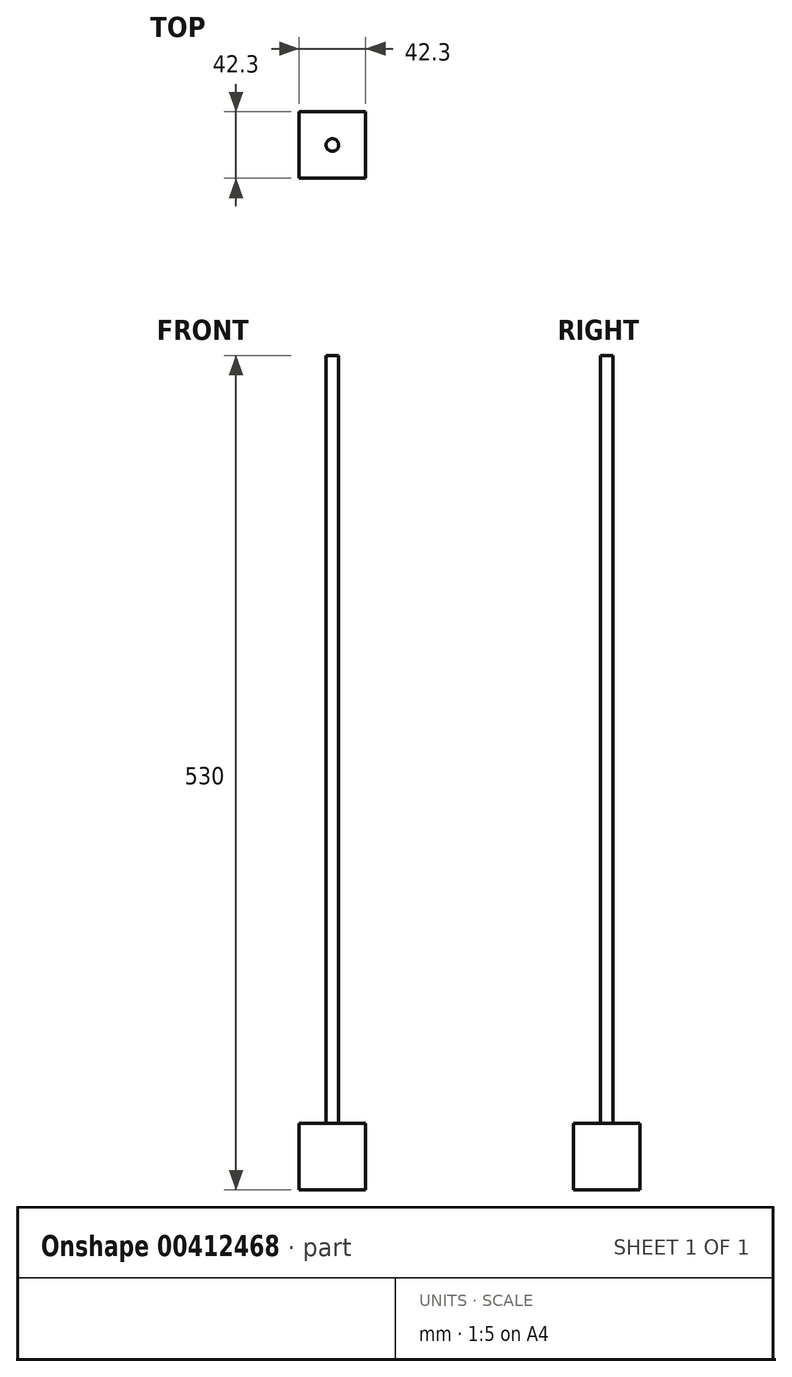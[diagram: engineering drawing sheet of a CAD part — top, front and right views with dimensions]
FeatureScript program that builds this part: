
annotation { "Feature Type Name" : "Feature", "Feature Type Description" : "" }
export const myFeature = defineFeature(function(context is Context, id is Id, definition is map)
    precondition{}
    {
        {
            var Q0;
            Q0=qCreatedBy(makeId("Top.planeOp"),FACE);
            var sketch = newSketch(context, id + "F0", { "sketchPlane" : qUnion([Q0])});
            skLineSegment(sketch, "E0.bottom", {"start": v(21.15, 21.15) * mm, "end": v(-21.15, 21.15) * mm});
            skLineSegment(sketch, "E0.top", {"start": v(21.15, -21.15) * mm, "end": v(-21.15, -21.15) * mm});
            skLineSegment(sketch, "E0.left", {"start": v(21.15, 21.15) * mm, "end": v(21.15, -21.15) * mm});
            skLineSegment(sketch, "E0.right", {"start": v(-21.15, 21.15) * mm, "end": v(-21.15, -21.15) * mm});
            skPoint(sketch, "E0.middle", {"position": v(0, 0) * mm});
            skCircle(sketch, "E1", {"center": v(0, 0) * mm, "radius": 4 * mm});
            skSolve(sketch);
        }
        {
            var Q0;
            Q0=makeQuery(id+"F0.imprint","IMPRINT",FACE,{"disambiguationData":[TD([[makeQuery(id+"F0.imprint","IMPRINT",EDGE,{"derivedFrom":sQuery(id+"F0.wireOp",EDGE,"E0.bottom")}),1.0]])]});
            extrude(context, id + "F1", {"entities" : qUnion([Q0]), "depth" : 42.3 * mm});
        }
        {
            var Q0;
            Q0=makeQuery(id+"F0.imprint","IMPRINT",FACE,{"disambiguationData":[TD([[makeQuery(id+"F0.imprint","IMPRINT",EDGE,{"derivedFrom":sQuery(id+"F0.wireOp",EDGE,"E1")}),1.0]])]});
            extrude(context, id + "F2", {"entities" : qUnion([Q0]), "operationType" : NewBodyOperationType.ADD, "depth" : 530 * mm});
        }
    });
